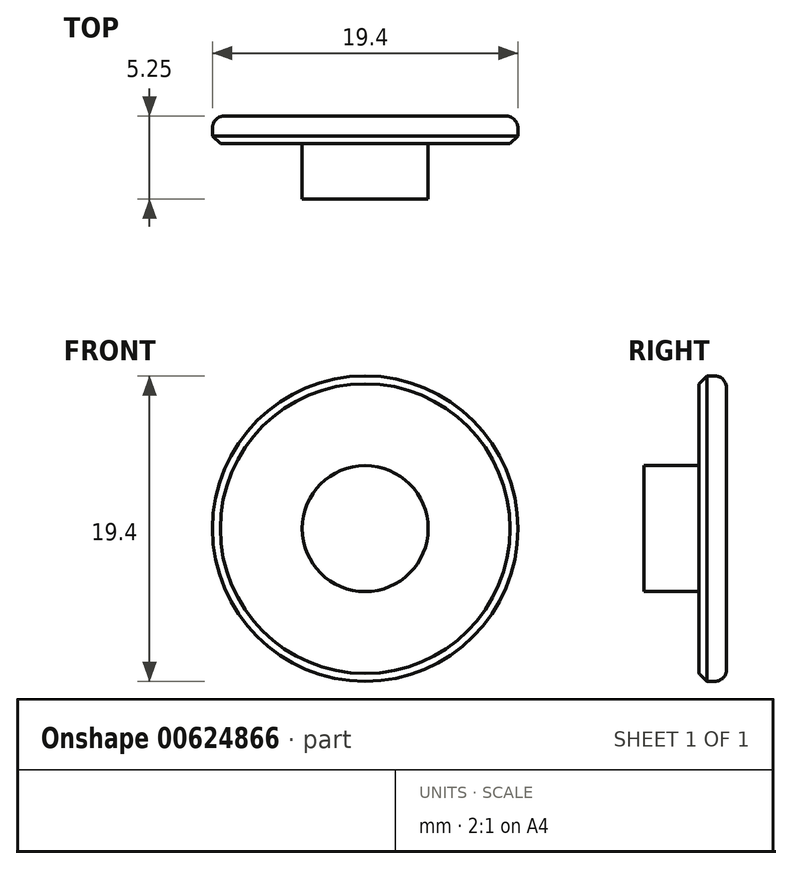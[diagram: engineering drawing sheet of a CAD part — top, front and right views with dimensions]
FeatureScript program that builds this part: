
annotation { "Feature Type Name" : "Feature", "Feature Type Description" : "" }
export const myFeature = defineFeature(function(context is Context, id is Id, definition is map)
    precondition{}
    {
        {
            var Q0;
            Q0=qCreatedBy(makeId("Front.planeOp"),FACE);
            var sketch = newSketch(context, id + "F0", { "sketchPlane" : qUnion([Q0])});
            skCircle(sketch, "E0", {"center": v(0, 0) * mm, "radius": 9.7 * mm});
            skCircle(sketch, "E1", {"center": v(0, 0) * mm, "radius": 4 * mm});
            skSolve(sketch);
        }
        {
            var Q0;
            Q0=makeQuery(id+"F0.imprint","IMPRINT",FACE,{"disambiguationData":[TD([[makeQuery(id+"F0.imprint","IMPRINT",EDGE,{"derivedFrom":sQuery(id+"F0.wireOp",EDGE,"LWpX59dz-4iZw-4IW6-pnXj-JfZNDJg1iGPD")}),1.0]])]});
            var Q1;
            Q1=makeQuery(id+"F0.imprint","IMPRINT",FACE,{"disambiguationData":[TD([[makeQuery(id+"F0.imprint","IMPRINT",EDGE,{"derivedFrom":sQuery(id+"F0.wireOp",EDGE,"E1")}),1.0]])]});
            extrude(context, id + "F1", {"entities" : qUnion([Q0, Q1]), "depth" : 5.25 * mm, "offsetDistance" : 25 * mm});
        }
        {
            var Q0;
            Q0=makeQuery(id+"F0.imprint","IMPRINT",FACE,{"disambiguationData":[TD([[makeQuery(id+"F0.imprint","IMPRINT",EDGE,{"derivedFrom":sQuery(id+"F0.wireOp",EDGE,"E0")}),1.0]])]});
            extrude(context, id + "F2", {"entities" : qUnion([Q0]), "operationType" : NewBodyOperationType.ADD, "depth" : 1.75 * mm, "offsetDistance" : 25 * mm});
        }
        {
            var Q0;
            Q0=makeQuery(id+"F2.opExtrude","CAP_EDGE",EDGE,{"disambiguationData":[OSD([sQuery(id+"F0.wireOp",EDGE,"E0")])],"isStart":false});
            chamfer(context, id + "F3", {"entities" : qUnion([Q0]), "width" : .5 * mm, "tangentPropagation" : true});
        }
        {
            var Q0;
            Q0=makeQuery(id+"F2.opExtrude","CAP_EDGE",EDGE,{"disambiguationData":[OSD([sQuery(id+"F0.wireOp",EDGE,"E0")])],"isStart":true});
            fillet(context, id + "F4", {"entities" : qUnion([Q0]), "radius" : .75 * mm, "tangentPropagation" : true, "allowEdgeOverflow" : false});
        }
    });
